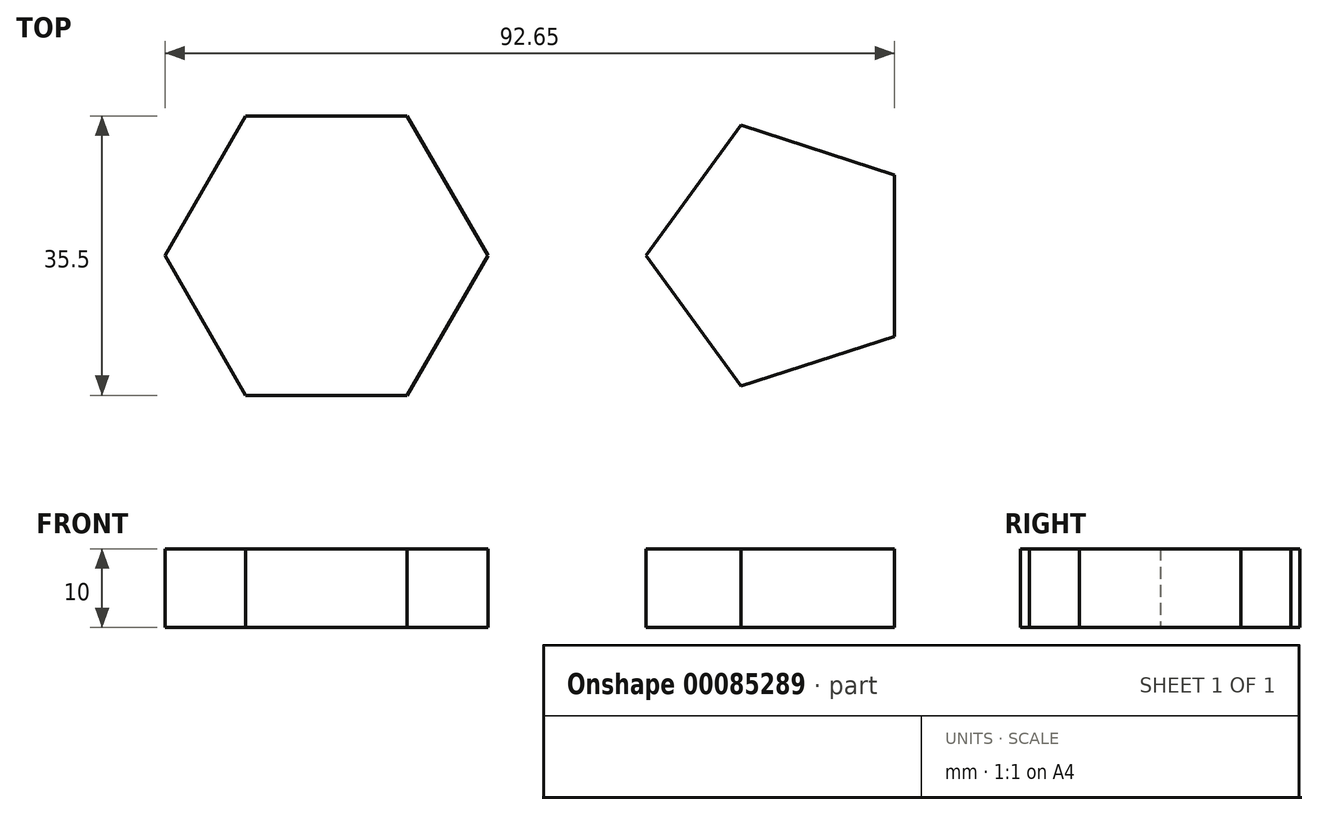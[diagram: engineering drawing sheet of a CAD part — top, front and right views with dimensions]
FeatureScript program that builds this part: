
annotation { "Feature Type Name" : "Feature", "Feature Type Description" : "" }
export const myFeature = defineFeature(function(context is Context, id is Id, definition is map)
    precondition{}
    {
        {
            var Q0;
            Q0=qCreatedBy(makeId("Top.planeOp"),FACE);
            var sketch = newSketch(context, id + "F0", { "sketchPlane" : qUnion([Q0])});
            skCircle(sketch, "E0.cCircle", {"center": v(-28.67, 0) * mm, "radius": 20.5 * mm, "construction": true});
            skLineSegment(sketch, "E0.0", {"start": v(-49.17, 0) * mm, "end": v(-38.92, 17.75) * mm});
            skLineSegment(sketch, "E0.1", {"start": v(-38.92, 17.75) * mm, "end": v(-18.42, 17.75) * mm});
            skLineSegment(sketch, "E0.2", {"start": v(-18.42, 17.75) * mm, "end": v(-8.17, 0) * mm});
            skLineSegment(sketch, "E0.3", {"start": v(-8.17, 0) * mm, "end": v(-18.42, -17.75) * mm});
            skLineSegment(sketch, "E0.4", {"start": v(-18.42, -17.75) * mm, "end": v(-38.92, -17.75) * mm});
            skLineSegment(sketch, "E0.5", {"start": v(-38.92, -17.75) * mm, "end": v(-49.17, 0) * mm});
            skCircle(sketch, "E1.cCircle", {"center": v(29.37, 0) * mm, "radius": 17.44 * mm, "construction": true});
            skLineSegment(sketch, "E1.0", {"start": v(11.93, 0) * mm, "end": v(23.98, 16.58) * mm});
            skLineSegment(sketch, "E1.1", {"start": v(23.98, 16.58) * mm, "end": v(43.48, 10.25) * mm});
            skLineSegment(sketch, "E1.2", {"start": v(43.48, 10.25) * mm, "end": v(43.48, -10.25) * mm});
            skLineSegment(sketch, "E1.3", {"start": v(43.48, -10.25) * mm, "end": v(23.98, -16.58) * mm});
            skLineSegment(sketch, "E1.4", {"start": v(23.98, -16.58) * mm, "end": v(11.93, 0) * mm});
            skSolve(sketch);
        }
        {
            var Q0;
            Q0=makeQuery(id+"F0.imprint","IMPRINT",FACE,{"disambiguationData":[TD([[makeQuery(id+"F0.imprint","IMPRINT",EDGE,{"derivedFrom":sQuery(id+"F0.wireOp",EDGE,"E0.0")}),-1.0]])]});
            var Q1;
            Q1=makeQuery(id+"F0.imprint","IMPRINT",FACE,{"disambiguationData":[TD([[makeQuery(id+"F0.imprint","IMPRINT",EDGE,{"derivedFrom":sQuery(id+"F0.wireOp",EDGE,"E1.0")}),-1.0]])]});
            extrude(context, id + "F1", {"entities" : qUnion([Q0, Q1]), "depth" : 10 * mm});
        }
    });
